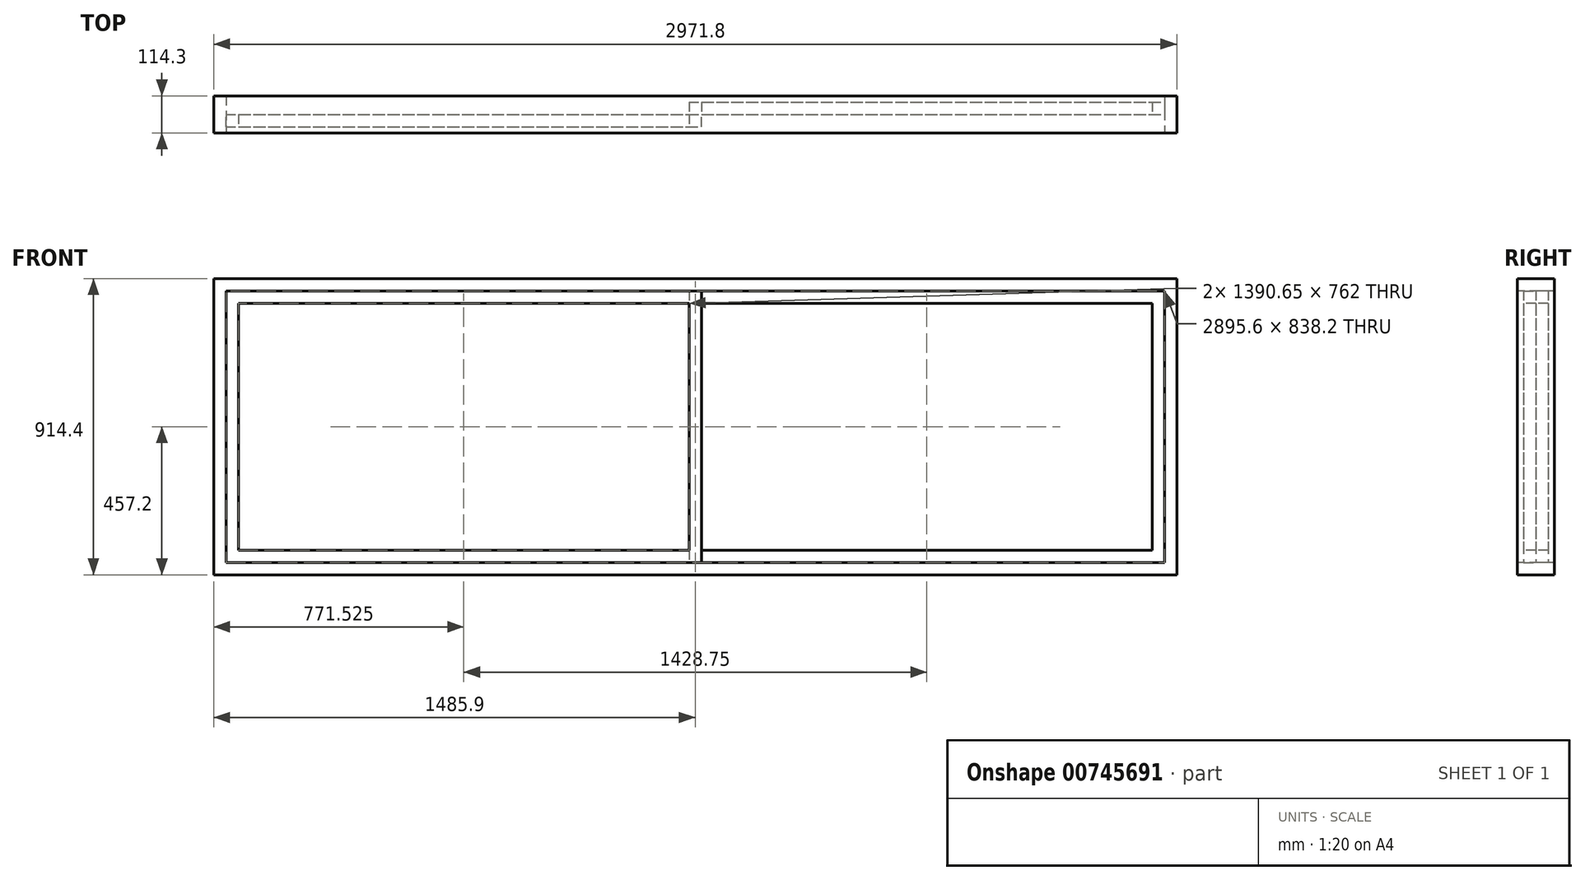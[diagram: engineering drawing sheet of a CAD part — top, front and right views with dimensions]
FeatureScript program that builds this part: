
annotation { "Feature Type Name" : "Feature", "Feature Type Description" : "" }
export const myFeature = defineFeature(function(context is Context, id is Id, definition is map)
    precondition{}
    {
        {
            var Q0;
            Q0=qCreatedBy(makeId("Front.planeOp"),FACE);
            var sketch = newSketch(context, id + "F0", { "sketchPlane" : qUnion([Q0])});
            skLineSegment(sketch, "E0.bottom", {"start": v(-1485.9, 457.2) * mm, "end": v(1485.9, 457.2) * mm});
            skLineSegment(sketch, "E0.top", {"start": v(-1485.9, -457.2) * mm, "end": v(1485.9, -457.2) * mm});
            skLineSegment(sketch, "E0.left", {"start": v(-1485.9, 457.2) * mm, "end": v(-1485.9, -457.2) * mm});
            skLineSegment(sketch, "E0.right", {"start": v(1485.9, 457.2) * mm, "end": v(1485.9, -457.2) * mm});
            skLineSegment(sketch, "E1", {"start": v(0, 457.2) * mm, "end": v(0, 0) * mm, "construction": true});
            skLineSegment(sketch, "E2", {"start": v(0, 0) * mm, "end": v(-1485.9, 0) * mm, "construction": true});
            skSolve(sketch);
        }
        {
            var Q0;
            Q0=makeQuery(id+"F0.imprint","IMPRINT",FACE,{"disambiguationData":[TD([[makeQuery(id+"F0.imprint","IMPRINT",EDGE,{"derivedFrom":sQuery(id+"F0.wireOp",EDGE,"E0.bottom")}),-1.0]])]});
            extrude(context, id + "F1", {"entities" : qUnion([Q0]), "endBound" : BoundingType.SYMMETRIC, "depth" : 114.3 * mm, "offsetDistance" : 25.4 * mm});
        }
        {
            var Q0;
            Q0=makeQuery(id+"F1.opExtrude","CAP_FACE",FACE,{"disambiguationData":[OSD([sQuery(id+"F0.wireOp",EDGE,"E0.bottom"),sQuery(id+"F0.wireOp",EDGE,"E0.top"),sQuery(id+"F0.wireOp",EDGE,"E0.left"),sQuery(id+"F0.wireOp",EDGE,"E0.right")])],"isStart":false});
            var sketch = newSketch(context, id + "F2", { "sketchPlane" : qUnion([Q0])});
            skLineSegment(sketch, "E3.bottom", {"start": v(-1447.8, 419.1) * mm, "end": v(1447.8, 419.1) * mm});
            skLineSegment(sketch, "E3.top", {"start": v(-1447.8, -419.1) * mm, "end": v(1447.8, -419.1) * mm});
            skLineSegment(sketch, "E3.left", {"start": v(-1447.8, 419.1) * mm, "end": v(-1447.8, -419.1) * mm});
            skLineSegment(sketch, "E3.right", {"start": v(1447.8, 419.1) * mm, "end": v(1447.8, -419.1) * mm});
            skSolve(sketch);
        }
        {
            var Q0;
            Q0=makeQuery(id+"F2.imprint","IMPRINT",FACE,{"disambiguationData":[TD([[makeQuery(id+"F2.imprint","IMPRINT",EDGE,{"derivedFrom":sQuery(id+"F2.wireOp",EDGE,"E3.bottom")}),-1.0]])]});
            extrude(context, id + "F3", {"entities" : qUnion([Q0]), "operationType" : NewBodyOperationType.REMOVE, "endBound" : BoundingType.THROUGH_ALL, "oppositeDirection" : true, "depth" : 25.4 * mm, "offsetDistance" : 25.4 * mm});
        }
        {
            var Q0;
            Q0=qCreatedBy(makeId("Front.planeOp"),FACE);
            var sketch = newSketch(context, id + "F4", { "sketchPlane" : qUnion([Q0])});
            skLineSegment(sketch, "E4.bottom", {"start": v(-1447.8, 419.1) * mm, "end": v(19.05, 419.1) * mm});
            skLineSegment(sketch, "E4.top", {"start": v(-1447.8, -419.1) * mm, "end": v(19.05, -419.1) * mm});
            skLineSegment(sketch, "E4.left", {"start": v(-1447.8, 419.1) * mm, "end": v(-1447.8, -419.1) * mm});
            skLineSegment(sketch, "E4.right", {"start": v(19.05, 419.1) * mm, "end": v(19.05, -419.1) * mm});
            skSolve(sketch);
        }
        {
            var Q0;
            Q0=makeQuery(id+"F4.imprint","IMPRINT",FACE,{"disambiguationData":[TD([[makeQuery(id+"F4.imprint","IMPRINT",EDGE,{"derivedFrom":sQuery(id+"F4.wireOp",EDGE,"E4.bottom")}),-1.0]])]});
            extrude(context, id + "F5", {"entities" : qUnion([Q0]), "depth" : 38.1 * mm, "offsetDistance" : 25.4 * mm});
        }
        {
            var Q0;
            Q0=makeQuery(id+"F5.opExtrude","CAP_FACE",FACE,{"disambiguationData":[OSD([sQuery(id+"F4.wireOp",EDGE,"E4.bottom"),sQuery(id+"F4.wireOp",EDGE,"E4.top"),sQuery(id+"F4.wireOp",EDGE,"E4.left"),sQuery(id+"F4.wireOp",EDGE,"E4.right")])],"isStart":false});
            var sketch = newSketch(context, id + "F6", { "sketchPlane" : qUnion([Q0])});
            skLineSegment(sketch, "E5.bottom", {"start": v(-1409.7, 381) * mm, "end": v(-19.05, 381) * mm});
            skLineSegment(sketch, "E5.top", {"start": v(-1409.7, -381) * mm, "end": v(-19.05, -381) * mm});
            skLineSegment(sketch, "E5.left", {"start": v(-1409.7, 381) * mm, "end": v(-1409.7, -381) * mm});
            skLineSegment(sketch, "E5.right", {"start": v(-19.05, 381) * mm, "end": v(-19.05, -381) * mm});
            skSolve(sketch);
        }
        {
            var Q0;
            Q0 = qSketchRegion(id + "F6", true);
            extrude(context, id + "F7", {"entities" : qUnion([Q0]), "operationType" : NewBodyOperationType.REMOVE, "endBound" : BoundingType.THROUGH_ALL, "oppositeDirection" : true, "depth" : 25.4 * mm, "offsetDistance" : 25.4 * mm});
        }
        {
            var Q0;
            Q0=qCreatedBy(makeId("Front.planeOp"),FACE);
            var sketch = newSketch(context, id + "F8", { "sketchPlane" : qUnion([Q0])});
            skLineSegment(sketch, "E6.bottom", {"start": v(-19.05, 419.1) * mm, "end": v(1447.8, 419.1) * mm});
            skLineSegment(sketch, "E6.top", {"start": v(-19.05, -419.1) * mm, "end": v(1447.8, -419.1) * mm});
            skLineSegment(sketch, "E6.left", {"start": v(-19.05, 419.1) * mm, "end": v(-19.05, -419.1) * mm});
            skLineSegment(sketch, "E6.right", {"start": v(1447.8, 419.1) * mm, "end": v(1447.8, -419.1) * mm});
            skSolve(sketch);
        }
        {
            var Q0;
            Q0 = qSketchRegion(id + "F8", true);
            extrude(context, id + "F9", {"entities" : qUnion([Q0]), "oppositeDirection" : true, "depth" : 38.1 * mm, "offsetDistance" : 25.4 * mm});
        }
        {
            var Q0;
            Q0=makeQuery(id+"F9.opExtrude","CAP_FACE",FACE,{"disambiguationData":[OSD([sQuery(id+"F8.wireOp",EDGE,"E6.bottom"),sQuery(id+"F8.wireOp",EDGE,"E6.top"),sQuery(id+"F8.wireOp",EDGE,"E6.left"),sQuery(id+"F8.wireOp",EDGE,"E6.right")])],"isStart":true});
            var sketch = newSketch(context, id + "F10", { "sketchPlane" : qUnion([Q0])});
            skLineSegment(sketch, "E7.bottom", {"start": v(19.05, 381) * mm, "end": v(1409.7, 381) * mm});
            skLineSegment(sketch, "E7.top", {"start": v(19.05, -381) * mm, "end": v(1409.7, -381) * mm});
            skLineSegment(sketch, "E7.left", {"start": v(19.05, 381) * mm, "end": v(19.05, -381) * mm});
            skLineSegment(sketch, "E7.right", {"start": v(1409.7, 381) * mm, "end": v(1409.7, -381) * mm});
            skSolve(sketch);
        }
        {
            var Q0;
            Q0 = qSketchRegion(id + "F10", true);
            extrude(context, id + "F11", {"entities" : qUnion([Q0]), "operationType" : NewBodyOperationType.REMOVE, "endBound" : BoundingType.THROUGH_ALL, "oppositeDirection" : true, "depth" : 25.4 * mm, "offsetDistance" : 25.4 * mm});
        }
    });
